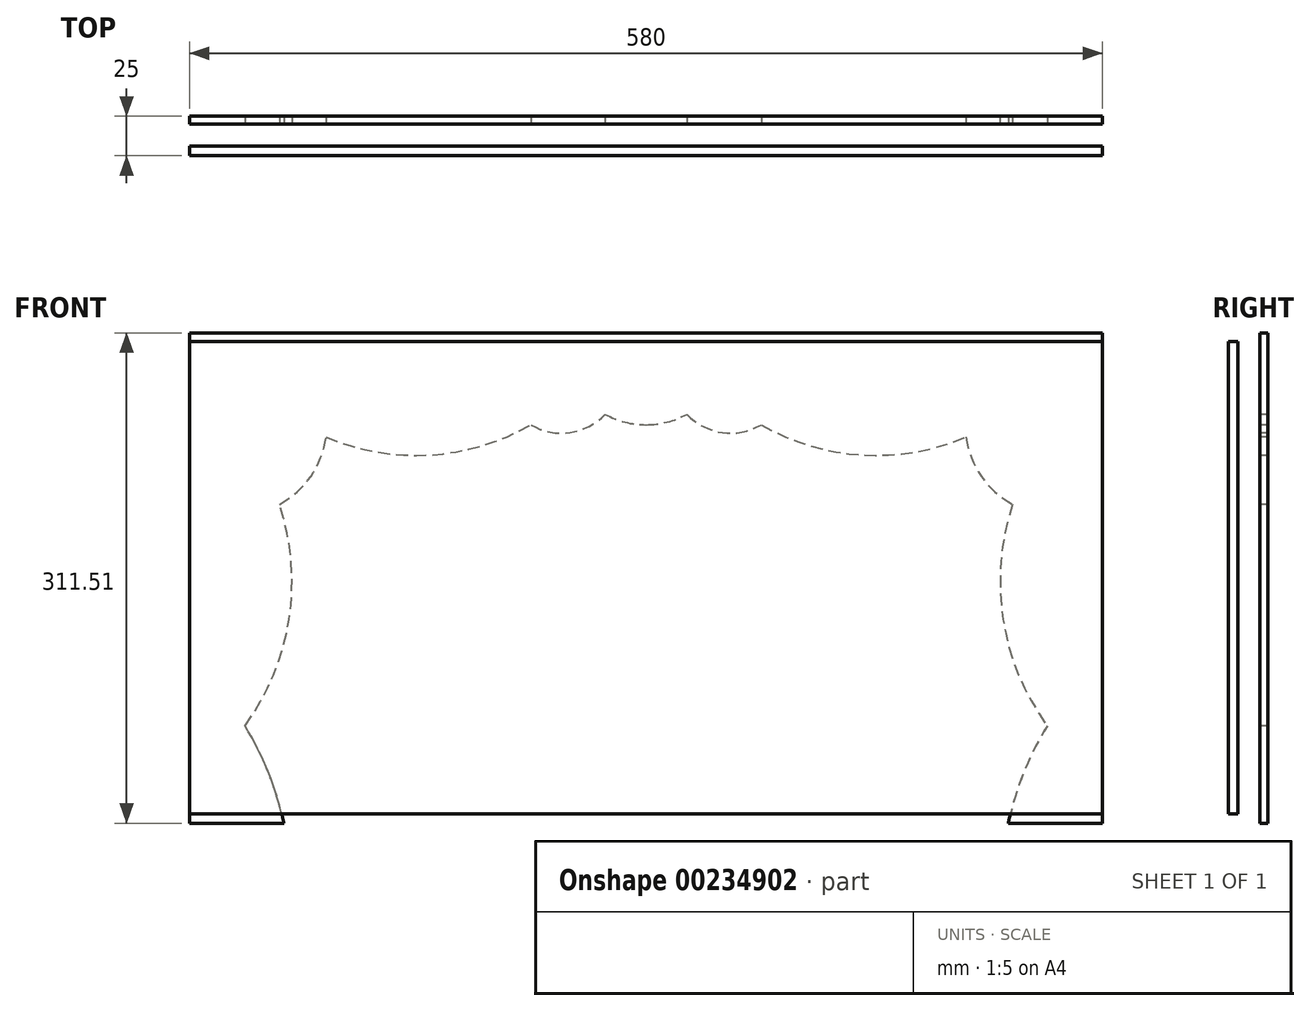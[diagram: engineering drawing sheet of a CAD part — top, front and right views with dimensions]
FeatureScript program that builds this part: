
annotation { "Feature Type Name" : "Feature", "Feature Type Description" : "" }
export const myFeature = defineFeature(function(context is Context, id is Id, definition is map)
    precondition{}
    {
        {
            var Q0;
            Q0=qCreatedBy(makeId("Front.planeOp"),FACE);
            var sketch = newSketch(context, id + "F0", { "sketchPlane" : qUnion([Q0])});
            skLineSegment(sketch, "E0.bottom", {"start": v(-290, 194.54) * mm, "end": v(290, 194.54) * mm});
            skLineSegment(sketch, "E0.top", {"start": v(-290, -105.46) * mm, "end": v(290, -105.46) * mm});
            skLineSegment(sketch, "E0.left", {"start": v(-290, 194.54) * mm, "end": v(-290, -105.46) * mm});
            skLineSegment(sketch, "E0.right", {"start": v(290, 194.54) * mm, "end": v(290, -105.46) * mm});
            skSolve(sketch);
        }
        {
            var Q0;
            Q0=makeQuery(id+"F0.imprint","IMPRINT",FACE,{"disambiguationData":[TD([[makeQuery(id+"F0.imprint","IMPRINT",EDGE,{"derivedFrom":sQuery(id+"F0.wireOp",EDGE,"E0.bottom")}),-1.0]])]});
            extrude(context, id + "F1", {"entities" : qUnion([Q0]), "oppositeDirection" : true, "depth" : 6 * mm});
        }
        {
            var Q0;
            Q0=qCreatedBy(makeId("Front.planeOp"),FACE);
            var sketch = newSketch(context, id + "F2", { "sketchPlane" : qUnion([Q0])});
            skLineSegment(sketch, "E1", {"start": v(-290, -111.5) * mm, "end": v(-290, 200) * mm});
            skLineSegment(sketch, "E2", {"start": v(-290, 200) * mm, "end": v(290, 200) * mm});
            skLineSegment(sketch, "E3", {"start": v(290, 200) * mm, "end": v(290, -111.5) * mm});
            skLineSegment(sketch, "E4", {"start": v(290, -111.5) * mm, "end": v(230.04, -111.5) * mm});
            skLineSegment(sketch, "E5", {"start": v(-290, -111.5) * mm, "end": v(-230.04, -111.5) * mm});
            skArc(sketch, "E6", {"start": v(-230.04, -111.5) * mm, "mid": v(-239.76, -79.5) * mm, "end": v(-254.8, -49.63) * mm});
            skArc(sketch, "E7", {"start": v(-254.8, -49.63) * mm, "mid": v(-226.75, 18.01) * mm, "end": v(-232.82, 90.99) * mm});
            skArc(sketch, "E8", {"start": v(-232.82, 90.99) * mm, "mid": v(-212.9, 108.87) * mm, "end": v(-203.14, 133.8) * mm});
            skArc(sketch, "E9", {"start": v(-203.14, 133.8) * mm, "mid": v(-137.24, 122.38) * mm, "end": v(-73.17, 141.55) * mm});
            skArc(sketch, "E10", {"start": v(-73.17, 141.55) * mm, "mid": v(-48.42, 136.6) * mm, "end": v(-26, 148.2) * mm});
            skArc(sketch, "E11", {"start": v(-26, 148.2) * mm, "mid": v(-13.42, 143.24) * mm, "end": v(0, 141.55) * mm});
            skArc(sketch, "E12.MirrorCS", {"start": v(26, 148.2) * mm, "mid": v(13.42, 143.24) * mm, "end": v(0, 141.55) * mm});
            skArc(sketch, "E13.MirrorCS", {"start": v(73.17, 141.55) * mm, "mid": v(48.42, 136.6) * mm, "end": v(26, 148.2) * mm});
            skArc(sketch, "E14.MirrorCS", {"start": v(203.14, 133.8) * mm, "mid": v(137.24, 122.38) * mm, "end": v(73.17, 141.55) * mm});
            skArc(sketch, "E15.MirrorCS", {"start": v(230.04, -111.5) * mm, "mid": v(239.76, -79.5) * mm, "end": v(254.8, -49.63) * mm});
            skArc(sketch, "E16.MirrorCS", {"start": v(254.8, -49.63) * mm, "mid": v(226.75, 18.01) * mm, "end": v(232.82, 90.99) * mm});
            skArc(sketch, "E17.MirrorCS", {"start": v(232.82, 90.99) * mm, "mid": v(212.9, 108.87) * mm, "end": v(203.14, 133.8) * mm});
            skPoint(sketch, "E18", {"position": v(-226.75, 18.01) * mm});
            skSolve(sketch);
        }
        {
            var Q0;
            Q0=makeQuery(id+"F2.imprint","IMPRINT",FACE,{"disambiguationData":[TD([[makeQuery(id+"F2.imprint","IMPRINT",EDGE,{"derivedFrom":sQuery(id+"F2.wireOp",EDGE,"E1")}),-1.0]])]});
            extrude(context, id + "F3", {"entities" : qUnion([Q0]), "oppositeDirection" : true, "depth" : 5 * mm});
        }
        {
            var Q0;
            Q0=makeQuery(id+"F3.opExtrude","SWEPT_BODY",BODY,{"disambiguationData":[OSD([sQuery(id+"F2.wireOp",EDGE,"E1"),sQuery(id+"F2.wireOp",EDGE,"E2"),sQuery(id+"F2.wireOp",EDGE,"E3"),sQuery(id+"F2.wireOp",EDGE,"E4"),sQuery(id+"F2.wireOp",EDGE,"E5"),sQuery(id+"F2.wireOp",EDGE,"E6"),sQuery(id+"F2.wireOp",EDGE,"E7"),sQuery(id+"F2.wireOp",EDGE,"E8"),sQuery(id+"F2.wireOp",EDGE,"E9"),sQuery(id+"F2.wireOp",EDGE,"E10"),sQuery(id+"F2.wireOp",EDGE,"E11"),sQuery(id+"F2.wireOp",EDGE,"E12.MirrorCS"),sQuery(id+"F2.wireOp",EDGE,"E13.MirrorCS"),sQuery(id+"F2.wireOp",EDGE,"E14.MirrorCS"),sQuery(id+"F2.wireOp",EDGE,"E15.MirrorCS"),sQuery(id+"F2.wireOp",EDGE,"E16.MirrorCS"),sQuery(id+"F2.wireOp",EDGE,"E17.MirrorCS")])]});
            transform(context, id + "F4", {"entities" : qUnion([Q0]), "transformType" : TransformType.TRANSLATION_3D, "dx" : 0 * mm, "dy" : 20 * mm, "dz" : 0 * mm, "makeCopy" : false});
        }
    });
